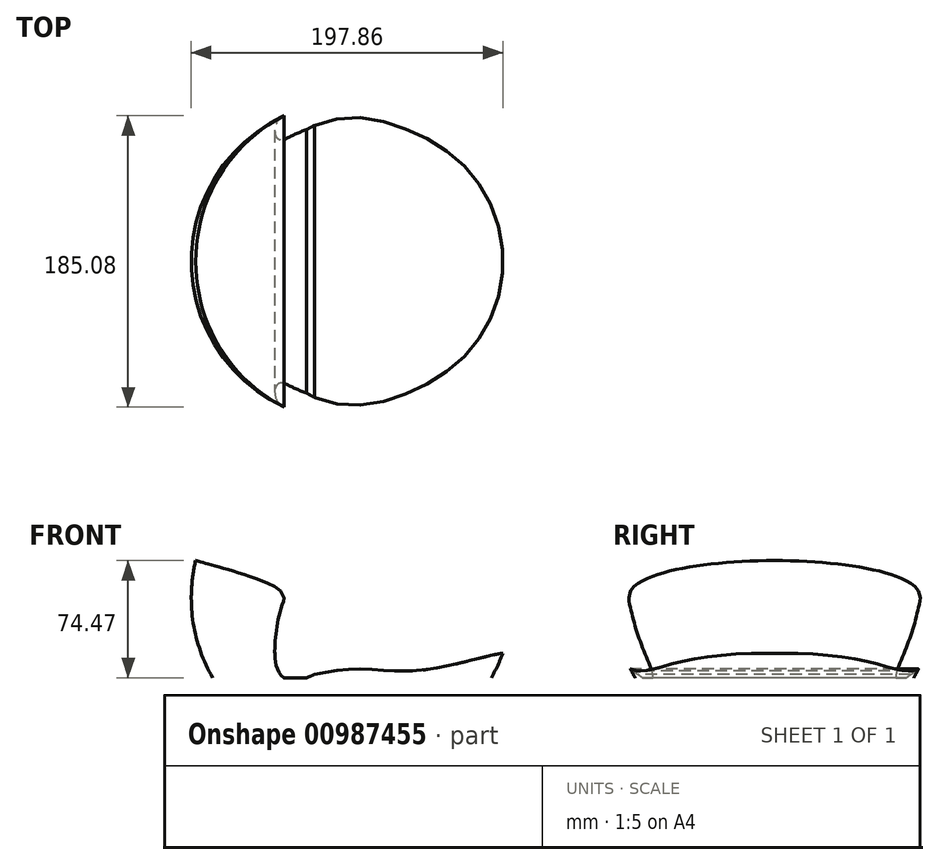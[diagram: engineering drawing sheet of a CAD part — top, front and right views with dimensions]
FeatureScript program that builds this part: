
annotation { "Feature Type Name" : "Feature", "Feature Type Description" : "" }
export const myFeature = defineFeature(function(context is Context, id is Id, definition is map)
    precondition{}
    {
        {
            var Q0;
            Q0=qCreatedBy(makeId("Front.planeOp"),FACE);
            var sketch = newSketch(context, id + "F0", { "sketchPlane" : qUnion([Q0])});
            skLineSegment(sketch, "E0", {"start": v(0, 0) * mm, "end": v(0, 203.2) * mm});
            skArc(sketch, "E1", {"start": v(0, 0) * mm, "mid": v(102.07, 101.6) * mm, "end": v(0, 203.2) * mm});
            skSolve(sketch);
        }
        {
            var Q0;
            Q0=makeQuery(id+"F0.imprint","IMPRINT",FACE,{"disambiguationData":[TD([[makeQuery(id+"F0.imprint","IMPRINT",EDGE,{"derivedFrom":sQuery(id+"F0.wireOp",EDGE,"E0")}),-1.0]])]});
            var Q1;
            Q1=sQuery(id+"F0.wireOp",EDGE,"E0");
            revolve(context, id + "F1", {"surfaceOperationType" : NewSurfaceOperationType.NEW, "entities" : qUnion([Q0]), "axis" : qUnion([Q1]), "revolveType" : RevolveType.FULL});
        }
        {
            var Q0;
            Q0=qCreatedBy(makeId("Front.planeOp"),FACE);
            var sketch = newSketch(context, id + "F2", { "sketchPlane" : qUnion([Q0])});
            skLineSegment(sketch, "E2.bottom", {"start": v(-181.04, 50.8) * mm, "end": v(181.04, 50.8) * mm});
            skLineSegment(sketch, "E2.top", {"start": v(-181.04, -50.8) * mm, "end": v(181.04, -50.8) * mm});
            skLineSegment(sketch, "E2.left", {"start": v(-181.04, 50.8) * mm, "end": v(-181.04, -50.8) * mm});
            skLineSegment(sketch, "E2.right", {"start": v(181.04, 50.8) * mm, "end": v(181.04, -50.8) * mm});
            skPoint(sketch, "E2.middle", {"position": v(0, 0) * mm});
            skSolve(sketch);
        }
        {
            var Q0;
            Q0=makeQuery(id+"F2.imprint","IMPRINT",FACE,{"disambiguationData":[TD([[makeQuery(id+"F2.imprint","IMPRINT",EDGE,{"derivedFrom":sQuery(id+"F2.wireOp",EDGE,"E2.bottom")}),-1.0]])]});
            extrude(context, id + "F3", {"entities" : qUnion([Q0]), "operationType" : NewBodyOperationType.REMOVE, "oppositeDirection" : true, "depth" : 152.4 * mm, "offsetDistance" : 25.4 * mm, "hasSecondDirection" : true, "secondDirectionOppositeDirection" : false, "secondDirectionDepth" : 152.4 * mm});
        }
        {
            var Q0;
            Q0=qCreatedBy(makeId("Front.planeOp"),FACE);
            var sketch = newSketch(context, id + "F4", { "sketchPlane" : qUnion([Q0])});
            skFitSpline(sketch, "E3", {"points": [v(-23.81, 52.9) * mm, v(-33.9, 49.42) * mm, v(-43.28, 50.81) * mm, v(-48.84, 63.33) * mm, v(-45.01, 94.96) * mm, v(-43.97, 104.7) * mm, v(-104.1, 126.59) * mm], "startDerivative": vector(-81.1, -35.65) * mm, "endDerivative": vector(-277.67, 75.56) * mm});
            skLineSegment(sketch, "E4", {"start": v(-104.1, 126.59) * mm, "end": v(-110.7, 44.9) * mm});
            skLineSegment(sketch, "E5", {"start": v(-110.7, 44.9) * mm, "end": v(68.3, 44.9) * mm});
            skFitSpline(sketch, "E6", {"points": [v(68.3, 44.9) * mm, v(79.77, 44.9) * mm, v(103.34, 59.74) * mm, v(103.34, 66.17) * mm, v(49.88, 56.37) * mm, v(0, 56.37) * mm, v(-23.81, 52.9) * mm], "startDerivative": vector(110, -17.91) * mm, "endDerivative": vector(-105.97, -21.3) * mm});
            skSolve(sketch);
        }
        {
            var Q0;
            Q0=makeQuery(id+"F4.imprint","IMPRINT",FACE,{"disambiguationData":[TD([[makeQuery(id+"F4.imprint","IMPRINT",EDGE,{"derivedFrom":sQuery(id+"F4.wireOp",EDGE,"E3")}),1.0]])]});
            extrude(context, id + "F5", {"entities" : qUnion([Q0]), "operationType" : NewBodyOperationType.REMOVE, "oppositeDirection" : true, "depth" : 152.4 * mm, "offsetDistance" : 25.4 * mm, "hasSecondDirection" : true, "secondDirectionOppositeDirection" : false, "secondDirectionDepth" : 152.4 * mm});
        }
        {
            var Q0;
            Q0=qCreatedBy(makeId("Front.planeOp"),FACE);
            cPlane(context, id + "F6", {"entities" : qUnion([Q0]), "cplaneType" : CPlaneType.OFFSET, "offset" : 101.6 * mm, "width" : 152.4 * mm, "height" : 152.4 * mm});
        }
        {
            var Q0;
            Q0=qCreatedBy(id+"F6.planeOp",FACE);
            var sketch = newSketch(context, id + "F7", { "sketchPlane" : qUnion([Q0])});
            skFitSpline(sketch, "E7", {"points": [v(-10.87, 72.27) * mm, v(-22.72, 79.5) * mm, v(-13.32, 88.06) * mm, v(-11.06, 88.51) * mm, v(20.19, 87.92) * mm, v(22.77, 87.2) * mm, v(22.77, 84.97) * mm, v(-7.31, 72.57) * mm, v(-10.87, 72.27) * mm]});
            skSolve(sketch);
        }
        {
            var Q0;
            Q0 = qSketchRegion(id + "F7", true);
            extrude(context, id + "F8", {"entities" : qUnion([Q0]), "operationType" : NewBodyOperationType.REMOVE, "endBound" : BoundingType.THROUGH_ALL, "oppositeDirection" : true, "depth" : 25.4 * mm, "offsetDistance" : 25.4 * mm, "hasSecondDirection" : true, "secondDirectionOppositeDirection" : false, "secondDirectionDepth" : 25.4 * mm});
        }
    });
